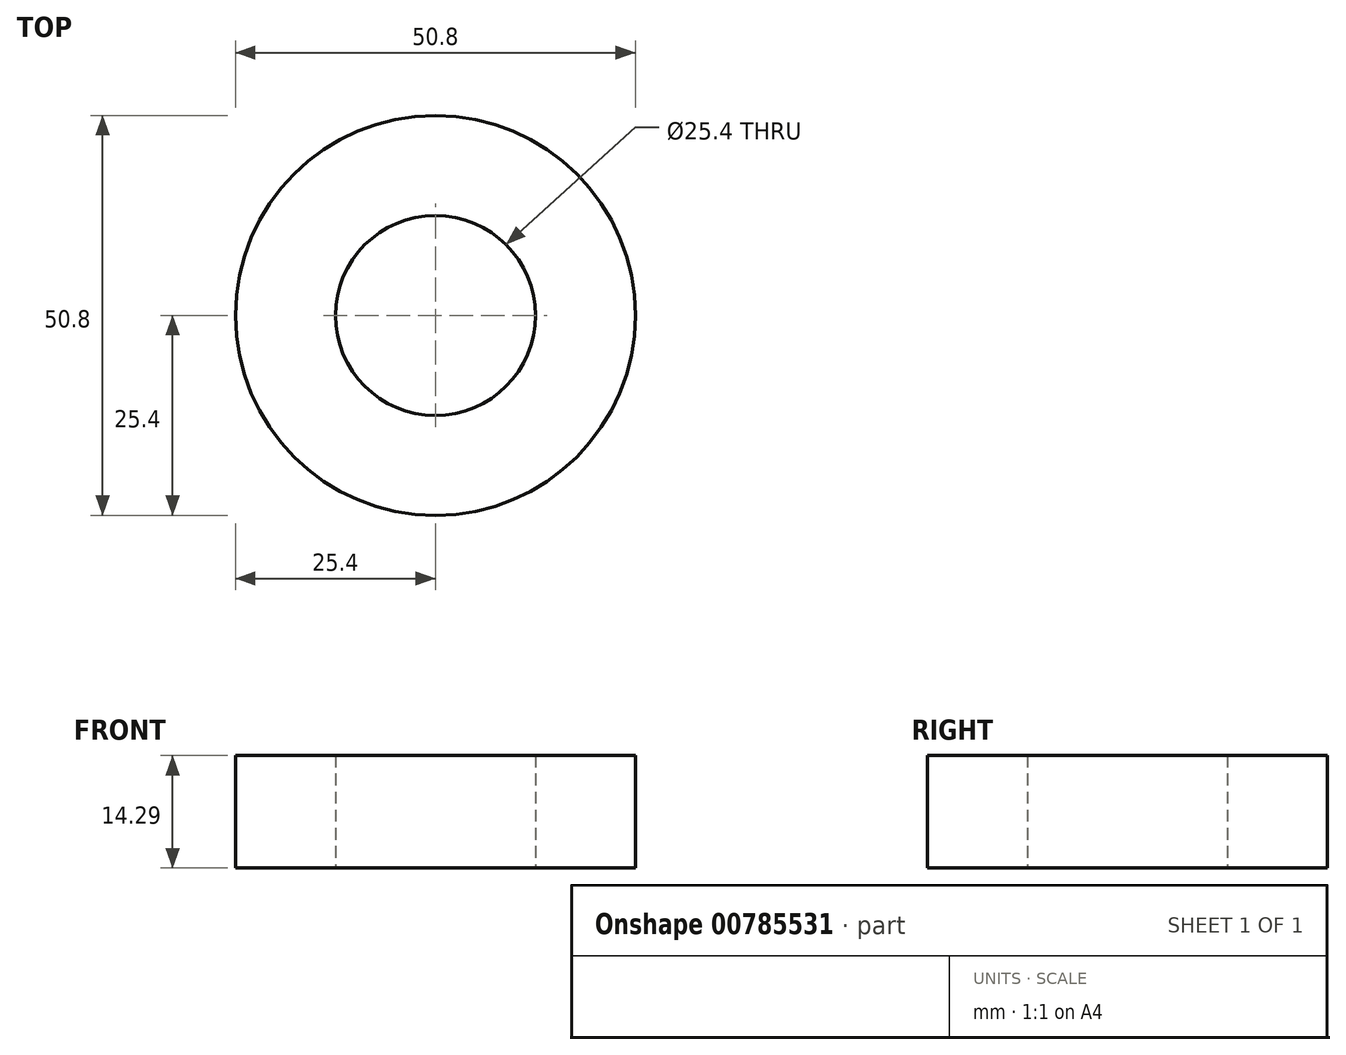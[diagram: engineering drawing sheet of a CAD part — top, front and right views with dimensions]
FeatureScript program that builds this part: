
annotation { "Feature Type Name" : "Feature", "Feature Type Description" : "" }
export const myFeature = defineFeature(function(context is Context, id is Id, definition is map)
    precondition{}
    {
        {
            var Q0;
            Q0=qCreatedBy(makeId("Top.planeOp"),FACE);
            var sketch = newSketch(context, id + "F0", { "sketchPlane" : qUnion([Q0])});
            skCircle(sketch, "E0", {"center": v(0, 0) * mm, "radius": 25.4 * mm});
            skCircle(sketch, "E1", {"center": v(0, 0) * mm, "radius": 12.7 * mm});
            skSolve(sketch);
        }
        {
            var Q0;
            Q0 = qSketchRegion(id + "F0", true);
            extrude(context, id + "F1", {"entities" : qUnion([Q0]), "depth" : 14.29 * mm, "offsetDistance" : 25 * mm});
        }
    });
